# Revit family: EB8
name_source: partatom
category: Generic Models
revit_build: Autodesk Revit LT 2017 (Build: 20160225_1515(x64)
units: mm (PartAtom-declared; Revit-internal decimal feet)

## family parameters
Always vertical = No
Can host rebar = No
Cut with Voids When Loaded = No
Part Type = Normal
Room Calculation Point = No
Round Connector Dimension = Use Diameter
Shared = No
Work Plane-Based = Yes

## types (1)
- NBS Standard Parameters
    BIMObjectName = Metpro_metprolibrary_electricalconnectionbox_connectorblock_brass
    Default Elevation = 1219 mm
    Description = EB8 - 8 Way Earth Block
    DurationUnit = year
    Finish = Nickel Plated
    Keynote = Comprises of Terminal Body and 2BA Screws
    ManufacturerName = Metpro Ltd
    ManufacturerURL = www.metpro.co.uk
    Material = Brass
    ModelReference = EB8
    NBSDescription = Electrical Connection Boxes
    NBSReference = 90-60-25/485
    NominalHeight = 19 mm
    NominalLength = 87 mm  [stored 0.285433 ft]
    NominalWidth = 20 mm  [stored 0.0656168 ft]
    ProductInformation = www.metpro.co.uk/pdf/eb8.pdf
    Shape = Rectangular
    Size = 0
    Uniclass2 = Pr_65_72_97_27
    Version = 1
    WarrantyDurationUnit = 1 year
    Weight = 0.142Kg

note: [stored X ft] marks values corroborated as IEEE doubles in the binary element streams (Revit-internal decimal feet)

## geometry (parser evidence)
native form markers: Sweep x2
no freeform markers — native parametric forms only
